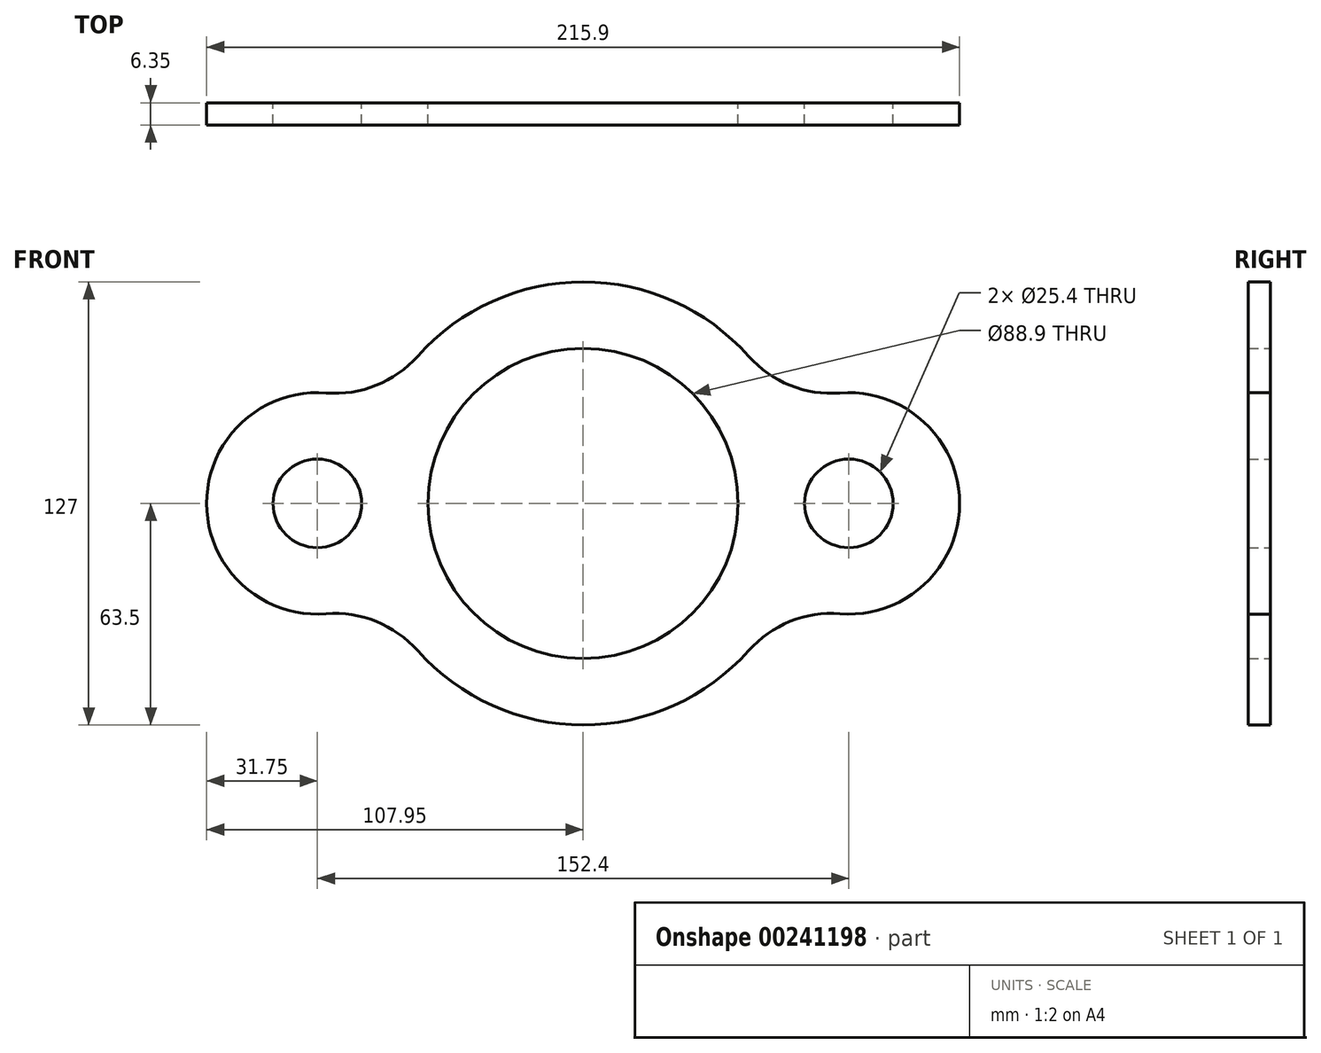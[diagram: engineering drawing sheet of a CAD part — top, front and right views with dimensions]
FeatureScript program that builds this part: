
annotation { "Feature Type Name" : "Feature", "Feature Type Description" : "" }
export const myFeature = defineFeature(function(context is Context, id is Id, definition is map)
    precondition{}
    {
        {
            var Q0;
            Q0=qCreatedBy(makeId("Front.planeOp"),FACE);
            var sketch = newSketch(context, id + "F0", { "sketchPlane" : qUnion([Q0])});
            skCircle(sketch, "E0", {"center": v(0, 0) * mm, "radius": 44.45 * mm});
            skArc(sketch, "E1", {"start": v(-47.45, -42.2) * mm, "mid": v(0, -63.5) * mm, "end": v(47.45, -42.2) * mm});
            skCircle(sketch, "E2", {"center": v(-76.2, 0) * mm, "radius": 12.7 * mm});
            skArc(sketch, "E3", {"start": v(-73.69, 31.65) * mm, "mid": v(-107.95, 0) * mm, "end": v(-73.69, -31.65) * mm});
            skPoint(sketch, "E4.visualSharp", {"position": v(-57.94, 25.98) * mm});
            skArc(sketch, "E4.filletArc", {"start": v(-73.69, 31.65) * mm, "mid": v(-59.33, 33.84) * mm, "end": v(-47.45, 42.2) * mm});
            skPoint(sketch, "E5.visualSharp", {"position": v(-57.94, -25.98) * mm});
            skArc(sketch, "E5.filletArc", {"start": v(-47.45, -42.2) * mm, "mid": v(-59.33, -33.84) * mm, "end": v(-73.69, -31.65) * mm});
            skArc(sketch, "E6.MirrorCS", {"start": v(73.69, 31.65) * mm, "mid": v(107.95, 0) * mm, "end": v(73.69, -31.65) * mm});
            skArc(sketch, "E7.MirrorCS", {"start": v(73.69, 31.65) * mm, "mid": v(59.33, 33.84) * mm, "end": v(47.45, 42.2) * mm});
            skArc(sketch, "E8.MirrorCS", {"start": v(47.45, -42.2) * mm, "mid": v(59.33, -33.84) * mm, "end": v(73.69, -31.65) * mm});
            skCircle(sketch, "E9.MirrorC", {"center": v(76.2, 0) * mm, "radius": 12.7 * mm});
            skArc(sketch, "E10.trimOffspring", {"start": v(47.45, 42.2) * mm, "mid": v(0, 63.5) * mm, "end": v(-47.45, 42.2) * mm});
            skSolve(sketch);
        }
        {
            var Q0;
            Q0 = qSketchRegion(id + "F0", true);
            extrude(context, id + "F1", {"entities" : qUnion([Q0]), "depth" : 6.35 * mm});
        }
    });
